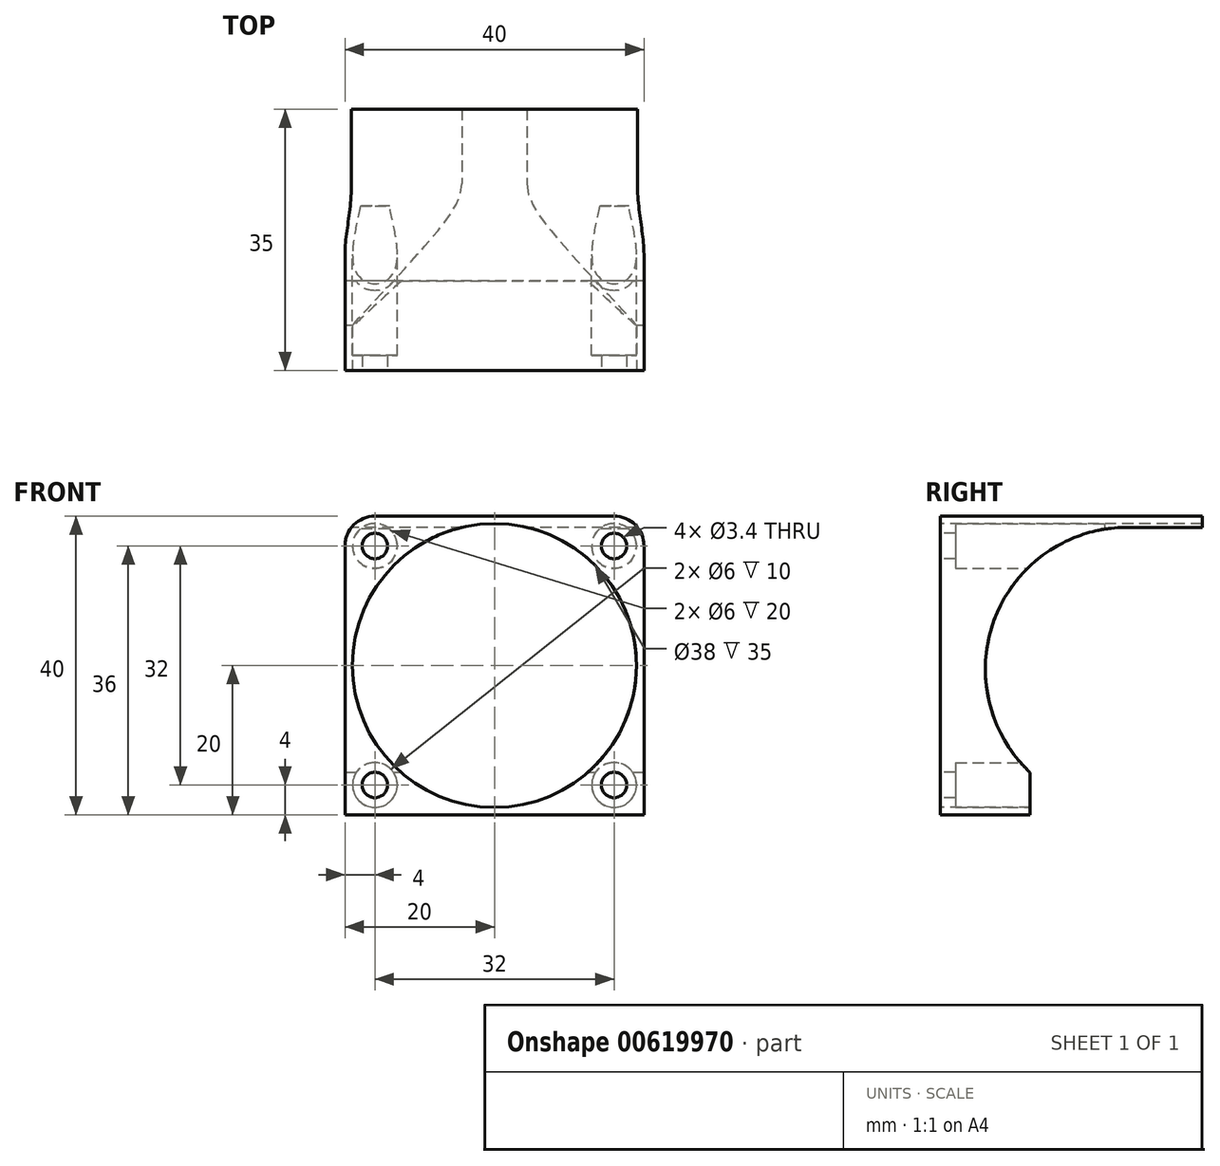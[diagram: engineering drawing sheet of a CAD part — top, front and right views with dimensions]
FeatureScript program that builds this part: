
annotation { "Feature Type Name" : "Feature", "Feature Type Description" : "" }
export const myFeature = defineFeature(function(context is Context, id is Id, definition is map)
    precondition{}
    {
        {
            var Q0;
            Q0=qCreatedBy(makeId("Front.planeOp"),FACE);
            var sketch = newSketch(context, id + "F0", { "sketchPlane" : qUnion([Q0])});
            skLineSegment(sketch, "E0.bottom", {"start": v(0, 0) * mm, "end": v(40, 0) * mm});
            skLineSegment(sketch, "E0.top", {"start": v(4, 40) * mm, "end": v(36, 40) * mm});
            skLineSegment(sketch, "E0.left", {"start": v(0, 0) * mm, "end": v(0, 36) * mm});
            skLineSegment(sketch, "E0.right", {"start": v(40, 0) * mm, "end": v(40, 36) * mm});
            skCircle(sketch, "E1", {"center": v(20, 20) * mm, "radius": 19 * mm});
            skCircle(sketch, "E2", {"center": v(4, 36) * mm, "radius": 1.7 * mm});
            skCircle(sketch, "E3", {"center": v(36, 36) * mm, "radius": 1.7 * mm});
            skCircle(sketch, "E4", {"center": v(4, 4) * mm, "radius": 1.7 * mm});
            skCircle(sketch, "E5", {"center": v(36, 4) * mm, "radius": 1.7 * mm});
            skPoint(sketch, "E6.visualSharp", {"position": v(0, 40) * mm});
            skArc(sketch, "E6.filletArc", {"start": v(4, 40) * mm, "mid": v(1.17, 38.83) * mm, "end": v(0, 36) * mm});
            skPoint(sketch, "E7.visualSharp", {"position": v(40, 40) * mm});
            skArc(sketch, "E7.filletArc", {"start": v(40, 36) * mm, "mid": v(38.83, 38.83) * mm, "end": v(36, 40) * mm});
            skSolve(sketch);
        }
        {
            var Q0;
            Q0=makeQuery(id+"F0.imprint","IMPRINT",FACE,{"disambiguationData":[TD([[makeQuery(id+"F0.imprint","IMPRINT",EDGE,{"derivedFrom":sQuery(id+"F0.wireOp",EDGE,"E0.bottom")}),1.0]])]});
            extrude(context, id + "F1", {"entities" : qUnion([Q0]), "depth" : -35 * mm, "offsetDistance" : 25 * mm});
        }
        {
            var Q0;
            Q0=makeQuery(id+"F1.opExtrude","SWEPT_FACE",FACE,{"disambiguationData":[OSD([sQuery(id+"F0.wireOp",EDGE,"E0.left")])]});
            var sketch = newSketch(context, id + "F2", { "sketchPlane" : qUnion([Q0])});
            skCircle(sketch, "E8", {"center": v(-25, 19.5) * mm, "radius": 19 * mm});
            skSolve(sketch);
        }
        {
            var Q0;
            {var subQ0=sQuery(id+"F2.wireOp",EDGE,"E8");var subQ1=sQuery(id+"F0.wireOp",EDGE,"E0.left");var subQ4=makeQuery(id+"F1.opExtrude","CAP_EDGE",EDGE,{"disambiguationData":[OSD([subQ1])],"isStart":false});var subQ5=makeQuery(id+"F2.imprint","INTERSECT",VERTEX,{"disambiguationData":[OD(0.0)],"derivedFrom":[subQ4,subQ0]});Q0=makeQuery(id+"F2.imprint","IMPRINT",FACE,{"disambiguationData":[TD([[makeQuery(id+"F2.imprint","IMPRINT",EDGE,{"disambiguationData":[TD([[subQ5,1.0]])],"derivedFrom":subQ4}),-1.0]])]});}
            var Q1;
            {var subQ0=sQuery(id+"F2.wireOp",EDGE,"E8");var subQ1=makeQuery(id+"F1.opExtrude","SWEPT_EDGE",EDGE,{"disambiguationData":[OSD([sQuery(id+"F0.wireOp",EDGE,"E0.left"),sQuery(id+"F0.wireOp",EDGE,"E6.filletArc")])]});var subQ2=makeQuery(id+"F2.imprint","INTERSECT",VERTEX,{"disambiguationData":[OD(0.0)],"derivedFrom":[subQ1,subQ0]});Q1=makeQuery(id+"F2.imprint","IMPRINT",FACE,{"disambiguationData":[TD([[makeQuery(id+"F2.imprint","IMPRINT",EDGE,{"disambiguationData":[TD([[subQ2,1.0]])],"derivedFrom":subQ0}),1.0]])]});}
            var Q2;
            {var subQ0=sQuery(id+"F2.wireOp",EDGE,"E8");var subQ1=makeQuery(id+"F1.opExtrude","CAP_EDGE",EDGE,{"disambiguationData":[OSD([sQuery(id+"F0.wireOp",EDGE,"E0.left")])],"isStart":false});var subQ2=makeQuery(id+"F2.imprint","INTERSECT",VERTEX,{"disambiguationData":[OD(0.0)],"derivedFrom":[subQ1,subQ0]});Q2=makeQuery(id+"F2.imprint","IMPRINT",FACE,{"disambiguationData":[TD([[makeQuery(id+"F2.imprint","IMPRINT",EDGE,{"disambiguationData":[TD([[subQ2,-1.0]])],"derivedFrom":subQ0}),1.0]])]});}
            var Q3;
            Q3=sQuery(id+"F2.wireOp",EDGE,"E8");
            extrude(context, id + "F3", {"entities" : qUnion([Q0, Q1, Q2]), "operationType" : NewBodyOperationType.REMOVE, "surfaceEntities" : qUnion([Q3]), "oppositeDirection" : true, "depth" : 41 * mm, "offsetDistance" : 25 * mm});
        }
        {
            var Q0;
            {var subQ0=sQuery(id+"F0.wireOp",EDGE,"E7.filletArc");var subQ1=sQuery(id+"F0.wireOp",EDGE,"E6.filletArc");var subQ2=sQuery(id+"F0.wireOp",EDGE,"E5");var subQ3=sQuery(id+"F0.wireOp",EDGE,"E4");var subQ4=sQuery(id+"F0.wireOp",EDGE,"E3");var subQ5=sQuery(id+"F0.wireOp",EDGE,"E2");var subQ6=sQuery(id+"F0.wireOp",EDGE,"E1");var subQ7=sQuery(id+"F0.wireOp",EDGE,"E0.right");var subQ8=sQuery(id+"F0.wireOp",EDGE,"E0.left");var subQ9=sQuery(id+"F0.wireOp",EDGE,"E0.top");var subQ10=sQuery(id+"F0.wireOp",EDGE,"E0.bottom");Q0=makeQuery(id+"F3.boolean.opBoolean","SPLIT",FACE,{"disambiguationData":[TD([makeQuery(id+"F1.opExtrude","SWEPT_FACE",FACE,{"disambiguationData":[OSD([subQ10])]}),makeQuery(id+"F1.opExtrude","CAP_FACE",FACE,{"disambiguationData":[OSD([subQ10,subQ9,subQ8,subQ7,subQ6,subQ5,subQ4,subQ3,subQ2,subQ1,subQ0])],"isStart":true}),makeQuery(id+"F1.opExtrude","CAP_FACE",FACE,{"disambiguationData":[OSD([subQ10,subQ9,subQ8,subQ7,subQ6,subQ5,subQ4,subQ3,subQ2,subQ1,subQ0])],"isStart":false}),makeQuery(id+"F1.opExtrude","SWEPT_FACE",FACE,{"disambiguationData":[OSD([subQ1])]}),makeQuery(id+"F3.opExtrude","SWEPT_FACE",FACE,{"disambiguationData":[OSD([sQuery(id+"F2.wireOp",EDGE,"E8")])]})])],"derivedFrom":makeQuery(id+"F1.opExtrude","SWEPT_FACE",FACE,{"disambiguationData":[OSD([subQ8])]})});}
            var sketch = newSketch(context, id + "F4", { "sketchPlane" : qUnion([Q0])});
            skLineSegment(sketch, "E9", {"start": v(0, 0) * mm, "end": v(-12, 0) * mm});
            skLineSegment(sketch, "E10.bottom", {"start": v(-12, 0) * mm, "end": v(-37.8, 0) * mm});
            skLineSegment(sketch, "E10.top", {"start": v(-12, 5.66) * mm, "end": v(-37.8, 5.66) * mm});
            skLineSegment(sketch, "E10.left", {"start": v(-12, 0) * mm, "end": v(-12, 5.66) * mm});
            skLineSegment(sketch, "E10.right", {"start": v(-37.8, 0) * mm, "end": v(-37.8, 5.66) * mm});
            skSolve(sketch);
        }
        {
            var Q0;
            {var subQ3=sQuery(id+"F2.wireOp",EDGE,"E8");var subQ5=sQuery(id+"F4.wireOp",EDGE,"E10.left");var subQ7=makeQuery(id+"F3.boolean.opBoolean","COPY",EDGE,{"disambiguationData":[OD(1.0)],"derivedFrom":makeQuery(id+"F3.opExtrude","CAP_EDGE",EDGE,{"disambiguationData":[OSD([subQ3])],"isStart":true})});var subQ8=makeQuery(id+"F4.imprint","INTERSECT",VERTEX,{"derivedFrom":[subQ7,subQ5]});Q0=makeQuery(id+"F4.imprint","IMPRINT",FACE,{"disambiguationData":[TD([[makeQuery(id+"F4.imprint","IMPRINT",EDGE,{"disambiguationData":[TD([[subQ8,1.0]])],"derivedFrom":subQ5}),1.0]])]});}
            extrude(context, id + "F5", {"entities" : qUnion([Q0]), "operationType" : NewBodyOperationType.REMOVE, "oppositeDirection" : true, "depth" : 41 * mm, "offsetDistance" : 25 * mm});
        }
        {
            var Q0;
            Q0=makeQuery(id+"F5.boolean.opBoolean","COPY",FACE,{"derivedFrom":makeQuery(id+"F5.opExtrude","SWEPT_FACE",FACE,{"disambiguationData":[OSD([sQuery(id+"F4.wireOp",EDGE,"E10.left")])]})});
            var sketch = newSketch(context, id + "F6", { "sketchPlane" : qUnion([Q0])});
            skCircle(sketch, "E11", {"center": v(-36, 4) * mm, "radius": 3 * mm});
            skCircle(sketch, "E12", {"center": v(-4, 4) * mm, "radius": 3 * mm});
            skSolve(sketch);
        }
        {
            var Q0;
            {var subQ1=sQuery(id+"F0.wireOp",EDGE,"E0.right");var subQ2=sQuery(id+"F0.wireOp",EDGE,"E5");var subQ3=makeQuery(id+"F1.opExtrude","SWEPT_FACE",FACE,{"disambiguationData":[OSD([subQ2])]});var subQ4=sQuery(id+"F4.wireOp",EDGE,"E10.left");var subQ5=makeQuery(id+"F5.opExtrude","SWEPT_FACE",FACE,{"disambiguationData":[OSD([subQ4])]});var subQ12=sQuery(id+"F0.wireOp",EDGE,"E1");var subQ15=makeQuery(id+"F5.boolean.opBoolean","INTERSECT",EDGE,{"derivedFrom":[makeQuery(id+"F3.boolean.opBoolean","SPLIT",FACE,{"disambiguationData":[TD([makeQuery(id+"F1.opExtrude","CAP_FACE",FACE,{"disambiguationData":[OSD([sQuery(id+"F0.wireOp",EDGE,"E0.bottom"),sQuery(id+"F0.wireOp",EDGE,"E0.top"),sQuery(id+"F0.wireOp",EDGE,"E0.left"),subQ1,subQ12,sQuery(id+"F0.wireOp",EDGE,"E2"),sQuery(id+"F0.wireOp",EDGE,"E3"),sQuery(id+"F0.wireOp",EDGE,"E4"),subQ2,sQuery(id+"F0.wireOp",EDGE,"E6.filletArc"),sQuery(id+"F0.wireOp",EDGE,"E7.filletArc")])],"isStart":true})])],"derivedFrom":subQ3}),subQ5]});Q0=makeQuery(id+"F6.imprint","IMPRINT",FACE,{"disambiguationData":[TD([[makeQuery(id+"F6.imprint","IMPRINT",EDGE,{"derivedFrom":subQ15}),-1.0]])]});}
            var Q1;
            {var subQ1=sQuery(id+"F0.wireOp",EDGE,"E0.right");var subQ2=sQuery(id+"F0.wireOp",EDGE,"E5");var subQ3=makeQuery(id+"F1.opExtrude","SWEPT_FACE",FACE,{"disambiguationData":[OSD([subQ2])]});var subQ4=sQuery(id+"F4.wireOp",EDGE,"E10.left");var subQ5=makeQuery(id+"F5.opExtrude","SWEPT_FACE",FACE,{"disambiguationData":[OSD([subQ4])]});var subQ12=sQuery(id+"F0.wireOp",EDGE,"E1");var subQ15=makeQuery(id+"F5.boolean.opBoolean","INTERSECT",EDGE,{"derivedFrom":[makeQuery(id+"F3.boolean.opBoolean","SPLIT",FACE,{"disambiguationData":[TD([makeQuery(id+"F1.opExtrude","CAP_FACE",FACE,{"disambiguationData":[OSD([sQuery(id+"F0.wireOp",EDGE,"E0.bottom"),sQuery(id+"F0.wireOp",EDGE,"E0.top"),sQuery(id+"F0.wireOp",EDGE,"E0.left"),subQ1,subQ12,sQuery(id+"F0.wireOp",EDGE,"E2"),sQuery(id+"F0.wireOp",EDGE,"E3"),sQuery(id+"F0.wireOp",EDGE,"E4"),subQ2,sQuery(id+"F0.wireOp",EDGE,"E6.filletArc"),sQuery(id+"F0.wireOp",EDGE,"E7.filletArc")])],"isStart":true})])],"derivedFrom":subQ3}),subQ5]});Q1=makeQuery(id+"F6.imprint","IMPRINT",FACE,{"disambiguationData":[TD([[makeQuery(id+"F6.imprint","IMPRINT",EDGE,{"derivedFrom":subQ15}),1.0]])]});}
            var Q2;
            {var subQ1=sQuery(id+"F0.wireOp",EDGE,"E0.left");var subQ2=sQuery(id+"F0.wireOp",EDGE,"E4");var subQ3=makeQuery(id+"F1.opExtrude","SWEPT_FACE",FACE,{"disambiguationData":[OSD([subQ2])]});var subQ7=sQuery(id+"F4.wireOp",EDGE,"E10.left");var subQ8=makeQuery(id+"F5.opExtrude","SWEPT_FACE",FACE,{"disambiguationData":[OSD([subQ7])]});var subQ12=sQuery(id+"F0.wireOp",EDGE,"E1");var subQ15=makeQuery(id+"F5.boolean.opBoolean","INTERSECT",EDGE,{"derivedFrom":[makeQuery(id+"F3.boolean.opBoolean","SPLIT",FACE,{"disambiguationData":[TD([makeQuery(id+"F1.opExtrude","CAP_FACE",FACE,{"disambiguationData":[OSD([sQuery(id+"F0.wireOp",EDGE,"E0.bottom"),sQuery(id+"F0.wireOp",EDGE,"E0.top"),subQ1,sQuery(id+"F0.wireOp",EDGE,"E0.right"),subQ12,sQuery(id+"F0.wireOp",EDGE,"E2"),sQuery(id+"F0.wireOp",EDGE,"E3"),subQ2,sQuery(id+"F0.wireOp",EDGE,"E5"),sQuery(id+"F0.wireOp",EDGE,"E6.filletArc"),sQuery(id+"F0.wireOp",EDGE,"E7.filletArc")])],"isStart":true})])],"derivedFrom":subQ3}),subQ8]});Q2=makeQuery(id+"F6.imprint","IMPRINT",FACE,{"disambiguationData":[TD([[makeQuery(id+"F6.imprint","IMPRINT",EDGE,{"derivedFrom":subQ15}),-1.0]])]});}
            var Q3;
            {var subQ1=sQuery(id+"F0.wireOp",EDGE,"E0.left");var subQ2=sQuery(id+"F0.wireOp",EDGE,"E4");var subQ3=makeQuery(id+"F1.opExtrude","SWEPT_FACE",FACE,{"disambiguationData":[OSD([subQ2])]});var subQ7=sQuery(id+"F4.wireOp",EDGE,"E10.left");var subQ8=makeQuery(id+"F5.opExtrude","SWEPT_FACE",FACE,{"disambiguationData":[OSD([subQ7])]});var subQ12=sQuery(id+"F0.wireOp",EDGE,"E1");var subQ15=makeQuery(id+"F5.boolean.opBoolean","INTERSECT",EDGE,{"derivedFrom":[makeQuery(id+"F3.boolean.opBoolean","SPLIT",FACE,{"disambiguationData":[TD([makeQuery(id+"F1.opExtrude","CAP_FACE",FACE,{"disambiguationData":[OSD([sQuery(id+"F0.wireOp",EDGE,"E0.bottom"),sQuery(id+"F0.wireOp",EDGE,"E0.top"),subQ1,sQuery(id+"F0.wireOp",EDGE,"E0.right"),subQ12,sQuery(id+"F0.wireOp",EDGE,"E2"),sQuery(id+"F0.wireOp",EDGE,"E3"),subQ2,sQuery(id+"F0.wireOp",EDGE,"E5"),sQuery(id+"F0.wireOp",EDGE,"E6.filletArc"),sQuery(id+"F0.wireOp",EDGE,"E7.filletArc")])],"isStart":true})])],"derivedFrom":subQ3}),subQ8]});Q3=makeQuery(id+"F6.imprint","IMPRINT",FACE,{"disambiguationData":[TD([[makeQuery(id+"F6.imprint","IMPRINT",EDGE,{"derivedFrom":subQ15}),1.0]])]});}
            extrude(context, id + "F7", {"entities" : qUnion([Q0, Q1, Q2, Q3]), "operationType" : NewBodyOperationType.REMOVE, "oppositeDirection" : true, "depth" : 10 * mm, "offsetDistance" : 25 * mm});
        }
        {
            var Q0;
            {var subQ0=sQuery(id+"F0.wireOp",EDGE,"E7.filletArc");var subQ1=sQuery(id+"F0.wireOp",EDGE,"E6.filletArc");var subQ2=sQuery(id+"F0.wireOp",EDGE,"E5");var subQ3=sQuery(id+"F0.wireOp",EDGE,"E4");var subQ4=sQuery(id+"F0.wireOp",EDGE,"E3");var subQ5=sQuery(id+"F0.wireOp",EDGE,"E2");var subQ6=sQuery(id+"F0.wireOp",EDGE,"E1");var subQ7=sQuery(id+"F0.wireOp",EDGE,"E0.right");var subQ8=sQuery(id+"F0.wireOp",EDGE,"E0.left");var subQ9=sQuery(id+"F0.wireOp",EDGE,"E0.top");var subQ10=sQuery(id+"F0.wireOp",EDGE,"E0.bottom");Q0=makeQuery(id+"F3.boolean.opBoolean","SPLIT",FACE,{"disambiguationData":[TD([makeQuery(id+"F1.opExtrude","SWEPT_FACE",FACE,{"disambiguationData":[OSD([subQ10])]}),makeQuery(id+"F1.opExtrude","CAP_FACE",FACE,{"disambiguationData":[OSD([subQ10,subQ9,subQ8,subQ7,subQ6,subQ5,subQ4,subQ3,subQ2,subQ1,subQ0])],"isStart":true}),makeQuery(id+"F1.opExtrude","CAP_FACE",FACE,{"disambiguationData":[OSD([subQ10,subQ9,subQ8,subQ7,subQ6,subQ5,subQ4,subQ3,subQ2,subQ1,subQ0])],"isStart":false}),makeQuery(id+"F1.opExtrude","SWEPT_FACE",FACE,{"disambiguationData":[OSD([subQ1])]}),makeQuery(id+"F3.opExtrude","SWEPT_FACE",FACE,{"disambiguationData":[OSD([sQuery(id+"F2.wireOp",EDGE,"E8")])]})])],"derivedFrom":makeQuery(id+"F1.opExtrude","SWEPT_FACE",FACE,{"disambiguationData":[OSD([subQ8])]})});}
            var sketch = newSketch(context, id + "F8", { "sketchPlane" : qUnion([Q0])});
            skLineSegment(sketch, "E13", {"start": v(-25, 38.5) * mm, "end": v(-50.57, 38.5) * mm});
            skLineSegment(sketch, "E14", {"start": v(-50.57, 38.5) * mm, "end": v(-50.57, 29.26) * mm});
            skLineSegment(sketch, "E15", {"start": v(-50.57, 29.26) * mm, "end": v(-25, 29.26) * mm});
            skLineSegment(sketch, "E16", {"start": v(-25, 38.5) * mm, "end": v(-25, 29.26) * mm});
            skSolve(sketch);
        }
        {
            var Q0;
            Q0=makeQuery(id+"F8.imprint","IMPRINT",FACE,{"disambiguationData":[TD([[makeQuery(id+"F8.imprint","IMPRINT",EDGE,{"derivedFrom":sQuery(id+"F8.wireOp",EDGE,"E13")}),1.0]])]});
            extrude(context, id + "F9", {"entities" : qUnion([Q0]), "operationType" : NewBodyOperationType.REMOVE, "oppositeDirection" : true, "depth" : 41 * mm, "offsetDistance" : 25 * mm});
        }
        {
            var Q0;
            Q0=makeQuery(id+"F5.boolean.opBoolean","COPY",FACE,{"derivedFrom":makeQuery(id+"F5.opExtrude","SWEPT_FACE",FACE,{"disambiguationData":[OSD([sQuery(id+"F4.wireOp",EDGE,"E10.left")])]})});
            var sketch = newSketch(context, id + "F10", { "sketchPlane" : qUnion([Q0])});
            skCircle(sketch, "E17", {"center": v(-36, 36) * mm, "radius": 3 * mm});
            skPoint(sketch, "E17.centerSnap0", {"position": v(-36, 1) * mm});
            skCircle(sketch, "E18", {"center": v(-4, 36) * mm, "radius": 3 * mm});
            skSolve(sketch);
        }
        {
            var Q0;
            Q0=makeQuery(id+"F10.imprint","IMPRINT",FACE,{"disambiguationData":[TD([[makeQuery(id+"F10.imprint","IMPRINT",EDGE,{"derivedFrom":sQuery(id+"F10.wireOp",EDGE,"E18")}),1.0]])]});
            var Q1;
            Q1=makeQuery(id+"F10.imprint","IMPRINT",FACE,{"disambiguationData":[TD([[makeQuery(id+"F10.imprint","IMPRINT",EDGE,{"derivedFrom":sQuery(id+"F10.wireOp",EDGE,"E17")}),1.0]])]});
            extrude(context, id + "F11", {"entities" : qUnion([Q0, Q1]), "operationType" : NewBodyOperationType.REMOVE, "oppositeDirection" : true, "depth" : 20 * mm, "offsetDistance" : 25 * mm, "symmetric" : true});
        }
    });
